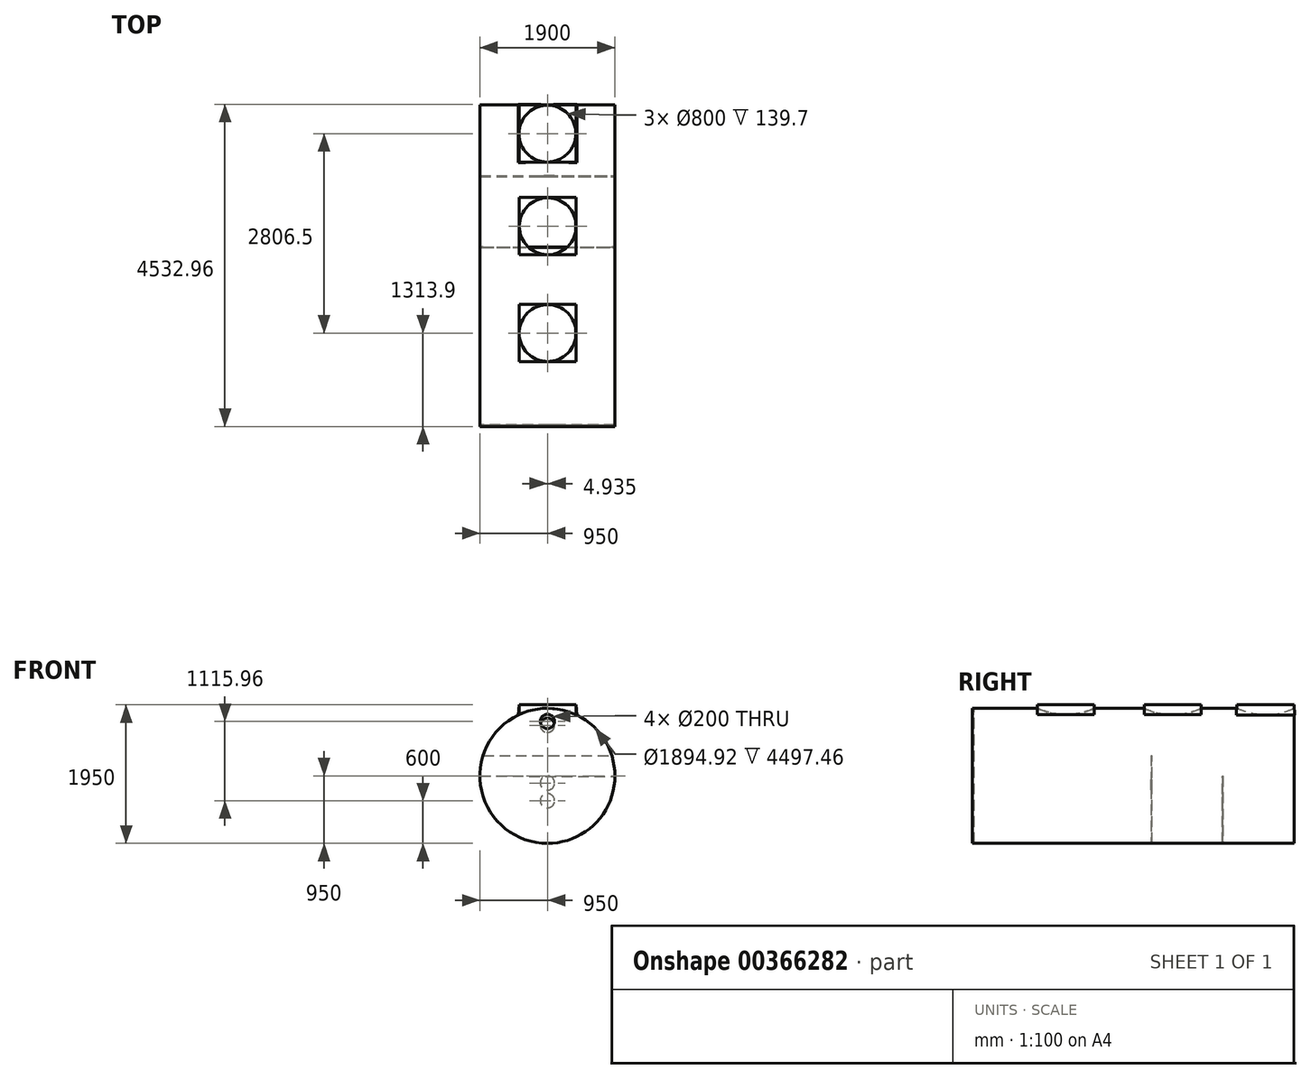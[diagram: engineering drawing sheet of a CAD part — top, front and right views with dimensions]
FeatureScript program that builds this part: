
annotation { "Feature Type Name" : "Feature", "Feature Type Description" : "" }
export const myFeature = defineFeature(function(context is Context, id is Id, definition is map)
    precondition{}
    {
        {
            var Q0;
            Q0=qCreatedBy(makeId("Front.planeOp"),FACE);
            var sketch = newSketch(context, id + "F0", { "sketchPlane" : qUnion([Q0])});
            skCircle(sketch, "E0", {"center": v(0, 0) * mm, "radius": 950 * mm});
            skSolve(sketch);
        }
        {
            var Q0;
            Q0=makeQuery(id+"F0.imprint","IMPRINT",FACE,{"disambiguationData":[TD([[makeQuery(id+"F0.imprint","IMPRINT",EDGE,{"derivedFrom":sQuery(id+"F0.wireOp",EDGE,"E0")}),1.0]])]});
            extrude(context, id + "F1", {"entities" : qUnion([Q0]), "depth" : 4500 * mm});
        }
        {
            var Q0;
            Q0=makeQuery(id+"F1.opExtrude","CAP_FACE",FACE,{"disambiguationData":[OSD([sQuery(id+"F0.wireOp",EDGE,"E0")])],"isStart":false});
            shell(context, id + "F2", {"entities" : qUnion([Q0]), "thickness" : 2.54 * mm});
        }
        {
            var Q0;
            Q0=qCreatedBy(makeId("Top.planeOp"),FACE);
            cPlane(context, id + "F3", {"entities" : qUnion([Q0]), "cplaneType" : CPlaneType.OFFSET, "offset" : 950 * mm, "oppositeDirection" : true, "width" : 152.4 * mm, "height" : 152.4 * mm});
        }
        {
            var Q0;
            Q0=qCreatedBy(id+"F3.planeOp",FACE);
            var sketch = newSketch(context, id + "F4", { "sketchPlane" : qUnion([Q0])});
            skLineSegment(sketch, "E1", {"start": v(0, 0) * mm, "end": v(0, -4512.62) * mm});
            skSolve(sketch);
        }
        {
            var Q0;
            Q0=qCreatedBy(makeId("Front.planeOp"),FACE);
            cPlane(context, id + "F5", {"entities" : qUnion([Q0]), "cplaneType" : CPlaneType.OFFSET, "offset" : 1000 * mm, "width" : 152.4 * mm, "height" : 152.4 * mm});
        }
        {
            var Q0;
            Q0=qCreatedBy(id+"F5.planeOp",FACE);
            var sketch = newSketch(context, id + "F6", { "sketchPlane" : qUnion([Q0])});
            skArc(sketch, "E2", {"start": v(-950, -3.05) * mm, "mid": v(-2.62, -950) * mm, "end": v(949.96, -8.3) * mm});
            skLineSegment(sketch, "E3", {"start": v(-950, -3.05) * mm, "end": v(949.96, -8.3) * mm});
            skSolve(sketch);
        }
        {
            var Q0;
            Q0 = qSketchRegion(id + "F6", true);
            extrude(context, id + "F7", {"entities" : qUnion([Q0]), "operationType" : NewBodyOperationType.ADD, "depth" : 10 * mm});
        }
        {
            var Q0;
            Q0=qCreatedBy(makeId("Front.planeOp"),FACE);
            cPlane(context, id + "F8", {"entities" : qUnion([Q0]), "cplaneType" : CPlaneType.OFFSET, "offset" : 2000 * mm, "width" : 152.4 * mm, "height" : 152.4 * mm});
        }
        {
            var Q0;
            Q0=qCreatedBy(id+"F8.planeOp",FACE);
            var sketch = newSketch(context, id + "F9", { "sketchPlane" : qUnion([Q0])});
            skLineSegment(sketch, "E4", {"start": v(-905.58, 287.08) * mm, "end": v(905.58, 287.08) * mm});
            skArc(sketch, "E5", {"start": v(-905.58, 287.08) * mm, "mid": v(0, -950) * mm, "end": v(905.58, 287.08) * mm});
            skSolve(sketch);
        }
        {
            var Q0;
            Q0 = qSketchRegion(id + "F9", true);
            extrude(context, id + "F10", {"entities" : qUnion([Q0]), "operationType" : NewBodyOperationType.ADD, "depth" : 10 * mm});
        }
        {
            var Q0;
            Q0=qCreatedBy(id+"F5.planeOp",FACE);
            var sketch = newSketch(context, id + "F11", { "sketchPlane" : qUnion([Q0])});
            skCircle(sketch, "E6", {"center": v(0, -350) * mm, "radius": 100 * mm});
            skSolve(sketch);
        }
        {
            var Q0;
            Q0 = qSketchRegion(id + "F11", true);
            extrude(context, id + "F12", {"entities" : qUnion([Q0]), "operationType" : NewBodyOperationType.REMOVE, "oppositeDirection" : true, "depth" : 10 * mm});
        }
        {
            var Q0;
            Q0=qCreatedBy(id+"F8.planeOp",FACE);
            var sketch = newSketch(context, id + "F13", { "sketchPlane" : qUnion([Q0])});
            skCircle(sketch, "E7", {"center": v(0, -100) * mm, "radius": 100 * mm});
            skSolve(sketch);
        }
        {
            var Q0;
            Q0 = qSketchRegion(id + "F13", true);
            extrude(context, id + "F14", {"entities" : qUnion([Q0]), "operationType" : NewBodyOperationType.REMOVE, "oppositeDirection" : true, "depth" : 10 * mm});
        }
        {
            var Q0;
            Q0=makeQuery(id+"F7.opExtrude","CAP_FACE",FACE,{"disambiguationData":[OSD([sQuery(id+"F6.wireOp",EDGE,"E2"),sQuery(id+"F6.wireOp",EDGE,"E3")])],"isStart":false});
            var sketch = newSketch(context, id + "F15", { "sketchPlane" : qUnion([Q0])});
            skCircle(sketch, "E8", {"center": v(0, -350) * mm, "radius": 100 * mm});
            skSolve(sketch);
        }
        {
            var Q0;
            Q0 = qSketchRegion(id + "F15", true);
            extrude(context, id + "F16", {"entities" : qUnion([Q0]), "operationType" : NewBodyOperationType.REMOVE, "oppositeDirection" : true, "depth" : 10 * mm});
        }
        {
            var Q0;
            Q0=makeQuery(id+"F10.opExtrude","CAP_FACE",FACE,{"disambiguationData":[OSD([sQuery(id+"F9.wireOp",EDGE,"E4"),sQuery(id+"F9.wireOp",EDGE,"E5")])],"isStart":false});
            var sketch = newSketch(context, id + "F17", { "sketchPlane" : qUnion([Q0])});
            skCircle(sketch, "E9", {"center": v(0, -100) * mm, "radius": 100 * mm});
            skSolve(sketch);
        }
        {
            var Q0;
            Q0 = qSketchRegion(id + "F17", true);
            extrude(context, id + "F18", {"entities" : qUnion([Q0]), "operationType" : NewBodyOperationType.REMOVE, "oppositeDirection" : true, "depth" : 10 * mm});
        }
        {
            var Q0;
            Q0=qCreatedBy(makeId("Top.planeOp"),FACE);
            cPlane(context, id + "F19", {"entities" : qUnion([Q0]), "cplaneType" : CPlaneType.OFFSET, "offset" : 1000 * mm, "width" : 152.4 * mm, "height" : 152.4 * mm});
        }
        {
            var Q0;
            Q0=qCreatedBy(id+"F19.planeOp",FACE);
            var sketch = newSketch(context, id + "F20", { "sketchPlane" : qUnion([Q0])});
            skLineSegment(sketch, "E10.bottom", {"start": v(-400, 0) * mm, "end": v(405, 0) * mm});
            skLineSegment(sketch, "E10.top", {"start": v(-400, -805) * mm, "end": v(405, -805) * mm});
            skLineSegment(sketch, "E10.left", {"start": v(-400, 0) * mm, "end": v(-400, -805) * mm});
            skLineSegment(sketch, "E10.right", {"start": v(405, 0) * mm, "end": v(405, -805) * mm});
            skSolve(sketch);
        }
        {
            var Q0;
            Q0 = qSketchRegion(id + "F20", true);
            var Q1;
            Q1=makeQuery(id+"F1.opExtrude","SWEPT_FACE",FACE,{"disambiguationData":[OSD([sQuery(id+"F0.wireOp",EDGE,"E0")])]});
            var Q2;
            Q2=makeQuery(id+"F1.opExtrude","SWEPT_BODY",BODY,{"disambiguationData":[OSD([sQuery(id+"F0.wireOp",EDGE,"E0")])]});
            extrude(context, id + "F21", {"entities" : qUnion([Q0]), "operationType" : NewBodyOperationType.ADD, "endBound" : BoundingType.UP_TO_SURFACE, "oppositeDirection" : true, "endBoundEntityFace" : qUnion([Q1]), "endBoundEntityBody" : qUnion([Q2]), "depth" : 25.4 * mm, "hasDraft" : true, "draftAngle" : 3 * degree});
        }
        {
            var Q0;
            Q0=qCreatedBy(id+"F19.planeOp",FACE);
            var sketch = newSketch(context, id + "F22", { "sketchPlane" : qUnion([Q0])});
            skLineSegment(sketch, "E11.bottom", {"start": v(-400, -1305) * mm, "end": v(405, -1305) * mm});
            skLineSegment(sketch, "E11.top", {"start": v(-400, -2110) * mm, "end": v(405, -2110) * mm});
            skLineSegment(sketch, "E11.left", {"start": v(-400, -1305) * mm, "end": v(-400, -2110) * mm});
            skLineSegment(sketch, "E11.right", {"start": v(405, -1305) * mm, "end": v(405, -2110) * mm});
            skSolve(sketch);
        }
        {
            var Q0;
            Q0 = qSketchRegion(id + "F22", true);
            extrude(context, id + "F23", {"entities" : qUnion([Q0]), "operationType" : NewBodyOperationType.ADD, "endBound" : BoundingType.UP_TO_NEXT, "oppositeDirection" : true, "depth" : 25.4 * mm});
        }
        {
            var Q0;
            Q0=qCreatedBy(id+"F19.planeOp",FACE);
            var sketch = newSketch(context, id + "F24", { "sketchPlane" : qUnion([Q0])});
            skLineSegment(sketch, "E12.bottom", {"start": v(-400, -2810) * mm, "end": v(405, -2810) * mm});
            skLineSegment(sketch, "E12.top", {"start": v(-400, -3615) * mm, "end": v(405, -3615) * mm});
            skLineSegment(sketch, "E12.left", {"start": v(-400, -2810) * mm, "end": v(-400, -3615) * mm});
            skLineSegment(sketch, "E12.right", {"start": v(405, -2810) * mm, "end": v(405, -3615) * mm});
            skSolve(sketch);
        }
        {
            var Q0;
            Q0 = qSketchRegion(id + "F24", true);
            extrude(context, id + "F25", {"entities" : qUnion([Q0]), "endBound" : BoundingType.UP_TO_NEXT, "oppositeDirection" : true, "depth" : 25.4 * mm});
        }
        {
            var Q0;
            Q0=qCreatedBy(makeId("Front.planeOp"),FACE);
            cPlane(context, id + "F26", {"entities" : qUnion([Q0]), "cplaneType" : CPlaneType.OFFSET, "offset" : 4500 * mm, "width" : 152.4 * mm, "height" : 152.4 * mm});
        }
        {
            var Q0;
            Q0=qCreatedBy(id+"F26.planeOp",FACE);
            var sketch = newSketch(context, id + "F27", { "sketchPlane" : qUnion([Q0])});
            skCircle(sketch, "E13", {"center": v(0, 0) * mm, "radius": 950 * mm});
            skSolve(sketch);
        }
        {
            var Q0;
            Q0 = qSketchRegion(id + "F27", true);
            extrude(context, id + "F28", {"entities" : qUnion([Q0]), "operationType" : NewBodyOperationType.ADD, "depth" : 25.4 * mm});
        }
        {
            var Q0;
            Q0=makeQuery(id+"F28.opExtrude","CAP_FACE",FACE,{"disambiguationData":[OSD([sQuery(id+"F27.wireOp",EDGE,"E13")])],"isStart":false});
            var sketch = newSketch(context, id + "F29", { "sketchPlane" : qUnion([Q0])});
            skCircle(sketch, "E14", {"center": v(0, 765.96) * mm, "radius": 100 * mm});
            skSolve(sketch);
        }
        {
            var Q0;
            Q0 = qSketchRegion(id + "F29", true);
            extrude(context, id + "F30", {"entities" : qUnion([Q0]), "operationType" : NewBodyOperationType.REMOVE, "oppositeDirection" : true, "depth" : 25.4 * mm});
        }
        {
            var Q0;
            Q0=makeQuery(id+"F1.opExtrude","CAP_FACE",FACE,{"disambiguationData":[OSD([sQuery(id+"F0.wireOp",EDGE,"E0")])],"isStart":true});
            var sketch = newSketch(context, id + "F31", { "sketchPlane" : qUnion([Q0])});
            skCircle(sketch, "E15", {"center": v(0, 712) * mm, "radius": 100 * mm});
            skSolve(sketch);
        }
        {
            var Q0;
            Q0 = qSketchRegion(id + "F31", true);
            extrude(context, id + "F32", {"entities" : qUnion([Q0]), "operationType" : NewBodyOperationType.REMOVE, "oppositeDirection" : true, "depth" : 25.4 * mm});
        }
        {
            var Q0;
            Q0=makeQuery(id+"F21.opExtrude","CAP_FACE",FACE,{"disambiguationData":[OSD([sQuery(id+"F20.wireOp",EDGE,"E10.bottom"),sQuery(id+"F20.wireOp",EDGE,"E10.top"),sQuery(id+"F20.wireOp",EDGE,"E10.left"),sQuery(id+"F20.wireOp",EDGE,"E10.right")])],"isStart":true});
            var sketch = newSketch(context, id + "F33", { "sketchPlane" : qUnion([Q0])});
            skCircle(sketch, "E16", {"center": v(0, -405) * mm, "radius": 400 * mm});
            skSolve(sketch);
        }
        {
            var Q0;
            Q0 = qSketchRegion(id + "F33", true);
            extrude(context, id + "F34", {"entities" : qUnion([Q0]), "operationType" : NewBodyOperationType.REMOVE, "oppositeDirection" : true, "depth" : 139.7 * mm});
        }
        {
            var Q0;
            Q0=makeQuery(id+"F23.opExtrude","CAP_FACE",FACE,{"disambiguationData":[OSD([sQuery(id+"F22.wireOp",EDGE,"E11.bottom"),sQuery(id+"F22.wireOp",EDGE,"E11.top"),sQuery(id+"F22.wireOp",EDGE,"E11.left"),sQuery(id+"F22.wireOp",EDGE,"E11.right")])],"isStart":true});
            var sketch = newSketch(context, id + "F35", { "sketchPlane" : qUnion([Q0])});
            skCircle(sketch, "E17", {"center": v(4.93, -1708.9) * mm, "radius": 400 * mm});
            skSolve(sketch);
        }
        {
            var Q0;
            Q0 = qSketchRegion(id + "F35", true);
            extrude(context, id + "F36", {"entities" : qUnion([Q0]), "operationType" : NewBodyOperationType.REMOVE, "oppositeDirection" : true, "depth" : 139.7 * mm});
        }
        {
            var Q0;
            Q0=makeQuery(id+"F25.opExtrude","CAP_FACE",FACE,{"disambiguationData":[OSD([sQuery(id+"F24.wireOp",EDGE,"E12.bottom"),sQuery(id+"F24.wireOp",EDGE,"E12.top"),sQuery(id+"F24.wireOp",EDGE,"E12.left"),sQuery(id+"F24.wireOp",EDGE,"E12.right")])],"isStart":true});
            var sketch = newSketch(context, id + "F37", { "sketchPlane" : qUnion([Q0])});
            skCircle(sketch, "E18", {"center": v(3.12, -3211.5) * mm, "radius": 400 * mm});
            skSolve(sketch);
        }
        {
            var Q0;
            Q0 = qSketchRegion(id + "F37", true);
            extrude(context, id + "F38", {"entities" : qUnion([Q0]), "operationType" : NewBodyOperationType.REMOVE, "oppositeDirection" : true, "depth" : 139.7 * mm});
        }
    });
